# Revit family: Deca_Cuba de piso redonda com mesa_Cubas Sobrepor_LC.1272
name_source: partatom
category: Plumbing Fixtures
units: mm (PartAtom-declared; Revit-internal decimal feet)

## family parameters
Cut with Voids When Loaded = No
Host = Face
Part Type = Normal
Room Calculation Point = No
Round Connector Dimension = Use Radius
Shared = No

## types (3) — shared parameters
Acompanha o Produto = Conjunto de instalação: parafusos de fixação e sifão corrugado
Aprovado por = quattroD
Atendimento ao Cliente = 0800-0117073
Categoria = CUBAS
Composição Anel Vedação = -
Composição Assento = -
Composição Básica = Argila, feldspato, caulim, vidrados e corantes inorgânicos.
Composição Componente = Liga de cobre (bronze e latão), elastômeros e plásticos de engenharia.
Consumo = -
Cor Interna = -
Cor Secundária = -
Cores Componente = Não Possui
Criado por = quattroD
Código Pai = LC.1272
Description = Cuba de piso redonda com mesa
Diâmetro Ponto de Esgoto = 0.03 m
Informações Complementares = -
Itens de Instalação = 1601.C; 1601.C.CLI; 1602.C; 1602.C.PLA
Linha = Cubas Sobrepor
Manufacturer = Deca
Norma = NBR-16728-1;NBR-16728-2
Peso Líquido (Kg) = 52.839
Pressão máx. funcionamento = -
Pressão mín. Aquec. Acúmulo = -
Pressão mín. Aquec. Passagem = -
Pressão mín. funcionamento = -
Raio Ponto de Esgoto = 0.01 m
Saída de Esgoto = Válvula Longa
Segmento = Banheiro Luxo
Tipo de dispositivo economizador = -
Tipo de mecanismo utilizado = -
Tipo de rosca de entrada = -
Tipo de rosca de saída = -
URL = www.deca.com.br
Vazão na Pressão máx. (L/min) = -
Vazão na Pressão mín. (L/min) = -
zero-valued in all types: Default Elevation, WFU

## per-type parameters (varying)
| type | Cor Principal | Material | Model |
| LC.1272.17_Branco | Branco | Deca_Branco | LC.1272.17 |
| LC.1272.22_Marrom Fosco | Marrom Fosco | Deca_Marrom Fosco | LC.1272.22 |
| LC.1272.95_Ébano | Ébano | Deca_Ébano | LC.1272.95 |

## geometry (parser evidence)
native form markers: Sweep x3
no freeform markers — native parametric forms only
